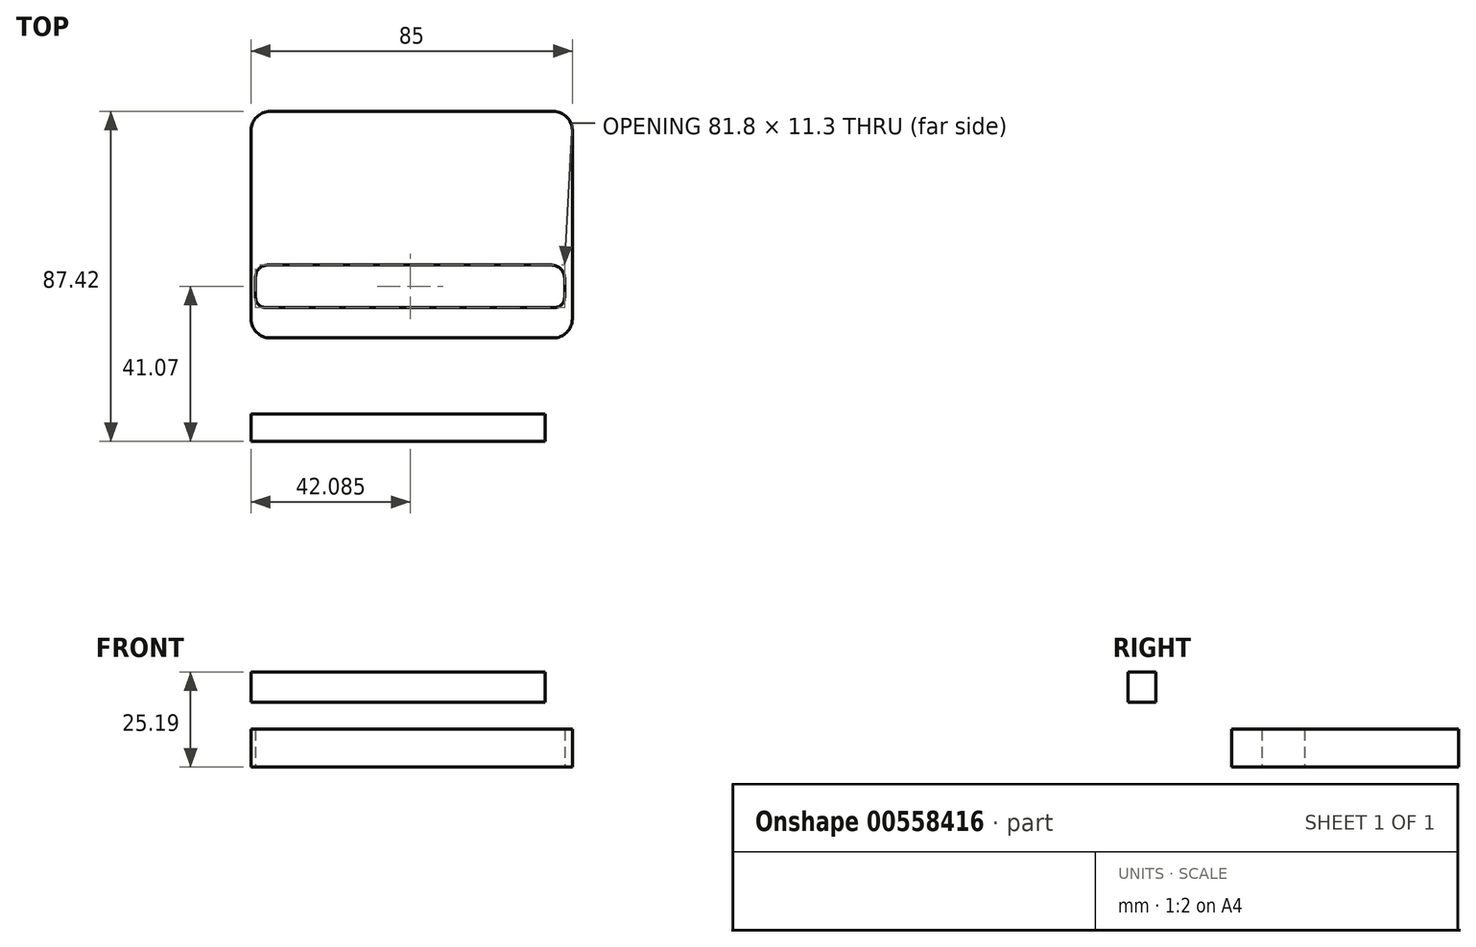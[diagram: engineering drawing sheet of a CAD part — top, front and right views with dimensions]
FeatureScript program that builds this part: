
annotation { "Feature Type Name" : "Feature", "Feature Type Description" : "" }
export const myFeature = defineFeature(function(context is Context, id is Id, definition is map)
    precondition{}
    {
        {
            var Q0;
            Q0=qCreatedBy(makeId("Top.planeOp"),FACE);
            var sketch = newSketch(context, id + "F0", { "sketchPlane" : qUnion([Q0])});
            skLineSegment(sketch, "E0.bottom", {"start": v(5, 0) * mm, "end": v(80, 0) * mm});
            skLineSegment(sketch, "E0.top", {"start": v(5, 60) * mm, "end": v(80, 60) * mm});
            skLineSegment(sketch, "E0.left", {"start": v(0, 5) * mm, "end": v(0, 55) * mm});
            skLineSegment(sketch, "E0.right", {"start": v(85, 5) * mm, "end": v(85, 55) * mm});
            skPoint(sketch, "E1.visualSharp", {"position": v(0, 60) * mm});
            skArc(sketch, "E1.filletArc", {"start": v(5, 60) * mm, "mid": v(1.46, 58.54) * mm, "end": v(0, 55) * mm});
            skPoint(sketch, "E2.visualSharp", {"position": v(0, 0) * mm});
            skArc(sketch, "E2.filletArc", {"start": v(0, 5) * mm, "mid": v(1.46, 1.46) * mm, "end": v(5, 0) * mm});
            skPoint(sketch, "E3.visualSharp", {"position": v(85, 0) * mm});
            skArc(sketch, "E3.filletArc", {"start": v(80, 0) * mm, "mid": v(83.54, 1.46) * mm, "end": v(85, 5) * mm});
            skPoint(sketch, "E4.visualSharp", {"position": v(85, 60) * mm});
            skArc(sketch, "E4.filletArc", {"start": v(85, 55) * mm, "mid": v(83.54, 58.54) * mm, "end": v(80, 60) * mm});
            skLineSegment(sketch, "E5.right", {"start": v(80.98, 10) * mm, "end": v(80.98, 17.3) * mm});
            skLineSegment(sketch, "E6.right", {"start": v(3.18, 10) * mm, "end": v(3.18, 17.3) * mm});
            skLineSegment(sketch, "E7", {"start": v(3.18, 17.3) * mm, "end": v(80.98, 17.3) * mm});
            skLineSegment(sketch, "E8", {"start": v(3.18, 10) * mm, "end": v(80.98, 10) * mm});
            skPoint(sketch, "E9", {"position": v(1.18, 8) * mm});
            skPoint(sketch, "E10", {"position": v(82.98, 19.3) * mm});
            skLineSegment(sketch, "E11.bottom", {"start": v(3.95, 8) * mm, "end": v(80.23, 8) * mm});
            skLineSegment(sketch, "E11.top", {"start": v(4.27, 19.3) * mm, "end": v(79.56, 19.3) * mm});
            skLineSegment(sketch, "E11.left", {"start": v(1.18, 10.76) * mm, "end": v(1.18, 16.21) * mm});
            skLineSegment(sketch, "E11.right", {"start": v(82.98, 10.75) * mm, "end": v(82.98, 15.87) * mm});
            skPoint(sketch, "E12.visualSharp", {"position": v(1.18, 19.3) * mm});
            skArc(sketch, "E12.filletArc", {"start": v(4.27, 19.3) * mm, "mid": v(2.09, 18.4) * mm, "end": v(1.18, 16.21) * mm});
            skArc(sketch, "E13.filletArc", {"start": v(82.98, 15.87) * mm, "mid": v(81.98, 18.3) * mm, "end": v(79.56, 19.3) * mm});
            skPoint(sketch, "E14.visualSharp", {"position": v(82.98, 8) * mm});
            skArc(sketch, "E14.filletArc", {"start": v(80.23, 8) * mm, "mid": v(82.18, 8.8) * mm, "end": v(82.98, 10.75) * mm});
            skArc(sketch, "E15.filletArc", {"start": v(1.18, 10.76) * mm, "mid": v(2, 8.8) * mm, "end": v(3.95, 8) * mm});
            skSolve(sketch);
        }
        {
            var Q0;
            Q0 = qSketchRegion(id + "F0", true);
            extrude(context, id + "F1", {"entities" : qUnion([Q0]), "depth" : 10 * mm, "offsetDistance" : 25 * mm});
        }
        {
            var Q0;
            Q0=qCreatedBy(makeId("Right.planeOp"),FACE);
            var sketch = newSketch(context, id + "F2", { "sketchPlane" : qUnion([Q0])});
            skLineSegment(sketch, "E16.bottom", {"start": v(-20.12, 17.19) * mm, "end": v(-27.42, 17.19) * mm});
            skLineSegment(sketch, "E16.top", {"start": v(-20.12, 25.19) * mm, "end": v(-27.42, 25.19) * mm});
            skLineSegment(sketch, "E16.left", {"start": v(-20.12, 17.19) * mm, "end": v(-20.12, 25.19) * mm});
            skLineSegment(sketch, "E16.right", {"start": v(-27.42, 17.19) * mm, "end": v(-27.42, 25.19) * mm});
            skSolve(sketch);
        }
        {
            var Q0;
            Q0 = qSketchRegion(id + "F2", true);
            extrude(context, id + "F3", {"entities" : qUnion([Q0]), "depth" : 77.8 * mm, "offsetDistance" : 25 * mm});
        }
    });
